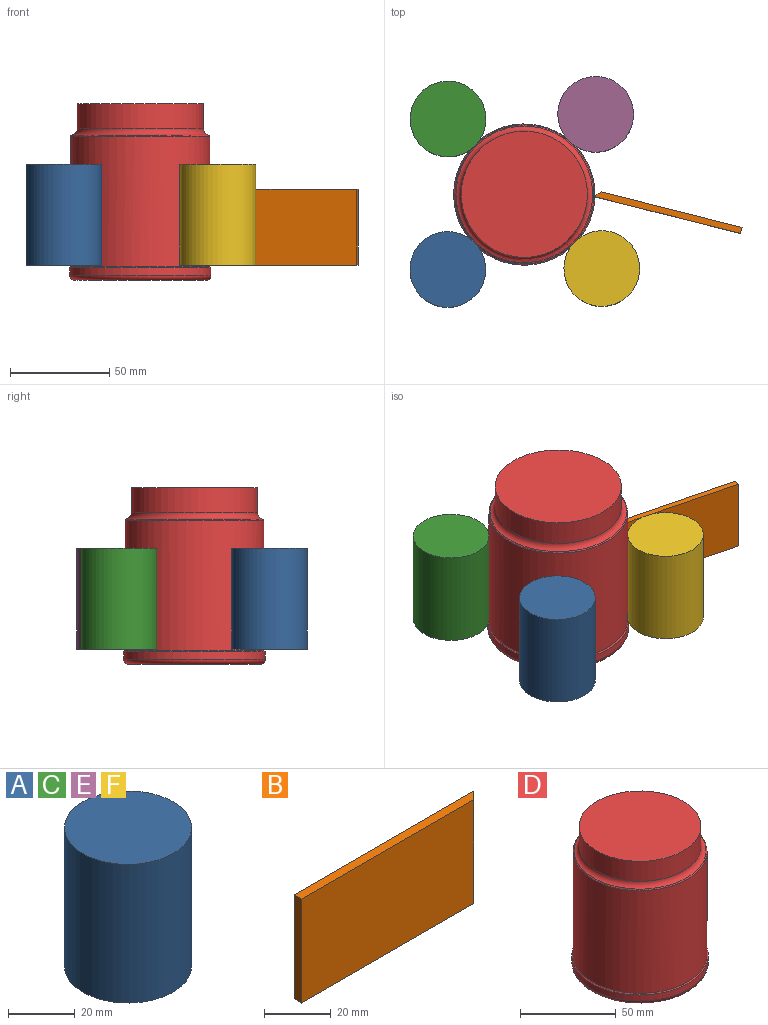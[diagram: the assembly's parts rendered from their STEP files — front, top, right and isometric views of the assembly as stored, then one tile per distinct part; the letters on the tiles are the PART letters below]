
ASSEMBLY  parts=6 mates=4
PART A: 3 faces, bbox 38.1x38.1x50.8 mm
  f0: cylinder r=19.05mm len=50.8mm, axis (0,0,-1), area 6080.5mm2, adj f1,f2
  f1: plane 38.1x38.1mm, normal (0,0,1), area 1140.1mm2, adj f0
  f2: plane 38.1x38.1mm, normal (0,0,-1), area 1140.1mm2, adj f0
PART B: 6 faces, bbox 76.2x3.2x38.1 mm
  f0: plane 76.2x3.18mm, normal (0,0,-1), area 236.9mm2, adj f2,f3,f4,f5
  f1: plane 76.2x3.18mm, normal (0,0,1), area 236.9mm2, adj f2,f3,f4,f5
  f2: plane 38.1x3.18mm, normal (-1,0,0), area 121mm2, adj f0,f1,f3,f4
  f3: plane 73.03x38.1mm, normal (0,-1,0), area 2782.3mm2, adj f0,f1,f2,f5
  f4: plane 76.2x38.1mm, normal (0,1,0), area 2903.2mm2, adj f0,f1,f2,f5
  f5: plane 38.1x3.18mm, normal (0.71,-0.71,0), area 171.1mm2, adj f0,f1,f3,f4
PART C: same geometry as A
PART D: 9 faces, bbox 78x78x88.9 mm
  f0: cylinder r=31.75mm len=63.5mm, axis (0,0,-1), area 2533.5mm2, adj f1,f7
  f1: plane 63.5x63.5mm, normal (0,0,1), area 3166.9mm2, adj f0
  f2: cylinder r=34.92mm len=69.85mm, axis (0,0,-1), area 14364.2mm2, adj f6,f8
  f3: cylinder r=35.56mm len=71.12mm, axis (0,0,-1), area 851.3mm2, adj f5,f6
  f4: plane 66.04x66.04mm, normal (0,0,-1), area 3425.3mm2, adj f5
  f5: torus R=33.02mm, axis (0,0,1), area 868.3mm2, adj f3,f4
  f6: torus R=35.56mm, axis (0,0,1), area 220.3mm2, adj f2,f3
  f7: torus R=34.92mm, axis (0,0,1), area 915.3mm2, adj f0,f8
  f8: torus R=34.29mm, axis (0,0,-1), area 194.5mm2, adj f2,f7
PART E: same geometry as A
PART F: same geometry as A
PLACE A rot(axis=(0,0,-1),135.5deg) t=(-38.5,-37.83,7.62)mm
PLACE B rot(axis=(0,0,1),165.8deg) t=(71.85,-10.34,26.67)mm
PLACE C rot(axis=(0,0,1),162.9deg) t=(-38.36,37.97,7.62)mm
PLACE D at identity
PLACE E rot(axis=(0,0,1),154.1deg) t=(35.94,40.27,7.62)mm
PLACE F rot(axis=(0,0,-1),139.7deg) t=(38.98,-37.33,7.62)mm
MATE planar E.f0 <-> D.f3  axis (0,0,-1) through (35.94,40.27,7.62)mm
MATE planar D.f3 <-> F.f0  axis (0,0,-1) through (0,0,0)mm
MATE planar B.f0 <-> F.f0  axis (0,0,-1) through (73,-9.01,7.62)mm
MATE planar D.f3 <-> C.f0  axis (0,0,-1) through (0,0,0)mm
